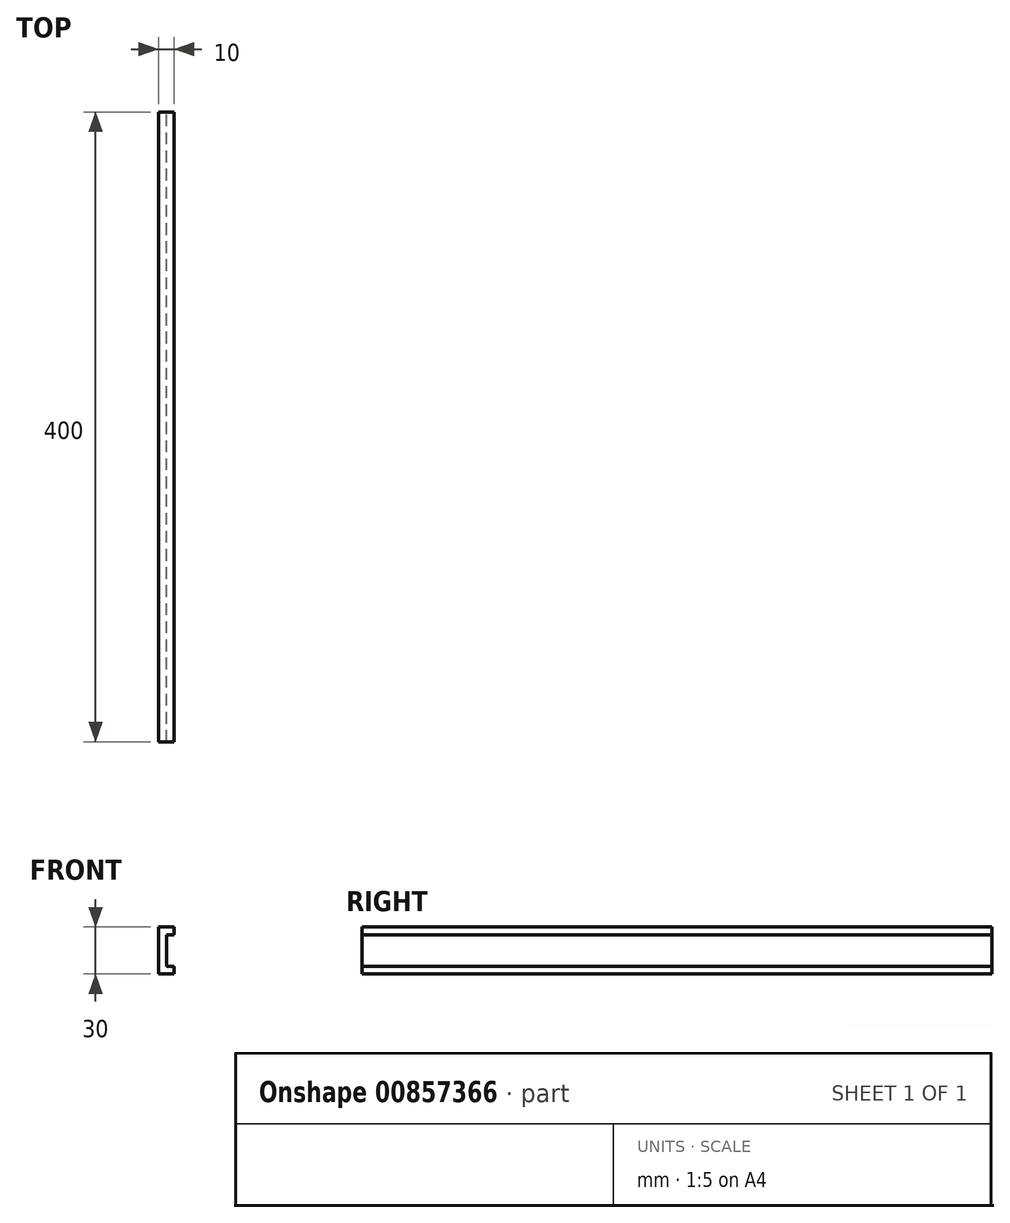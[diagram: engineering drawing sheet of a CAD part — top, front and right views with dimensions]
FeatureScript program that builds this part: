
annotation { "Feature Type Name" : "Feature", "Feature Type Description" : "" }
export const myFeature = defineFeature(function(context is Context, id is Id, definition is map)
    precondition{}
    {
        {
            var Q0;
            Q0=qCreatedBy(makeId("Front.planeOp"),FACE);
            var sketch = newSketch(context, id + "F0", { "sketchPlane" : qUnion([Q0])});
            skLineSegment(sketch, "E0", {"start": v(0, 0) * mm, "end": v(10, 0) * mm});
            skLineSegment(sketch, "E1", {"start": v(10, 0) * mm, "end": v(10, 5) * mm});
            skLineSegment(sketch, "E2", {"start": v(10, 5) * mm, "end": v(5, 5) * mm});
            skLineSegment(sketch, "E3", {"start": v(5, 5) * mm, "end": v(5, 25) * mm});
            skLineSegment(sketch, "E4", {"start": v(5, 25) * mm, "end": v(10, 25) * mm});
            skLineSegment(sketch, "E5", {"start": v(10, 25) * mm, "end": v(10, 30) * mm});
            skLineSegment(sketch, "E6", {"start": v(10, 30) * mm, "end": v(0, 30) * mm});
            skLineSegment(sketch, "E7", {"start": v(0, 30) * mm, "end": v(0, 0) * mm});
            skSolve(sketch);
        }
        {
            var Q0;
            Q0=makeQuery(id+"F0.imprint","IMPRINT",FACE,{"disambiguationData":[TD([[makeQuery(id+"F0.imprint","IMPRINT",EDGE,{"derivedFrom":sQuery(id+"F0.wireOp",EDGE,"E0")}),1.0]])]});
            extrude(context, id + "F1", {"entities" : qUnion([Q0]), "depth" : 400 * mm, "offsetDistance" : 25 * mm});
        }
    });
